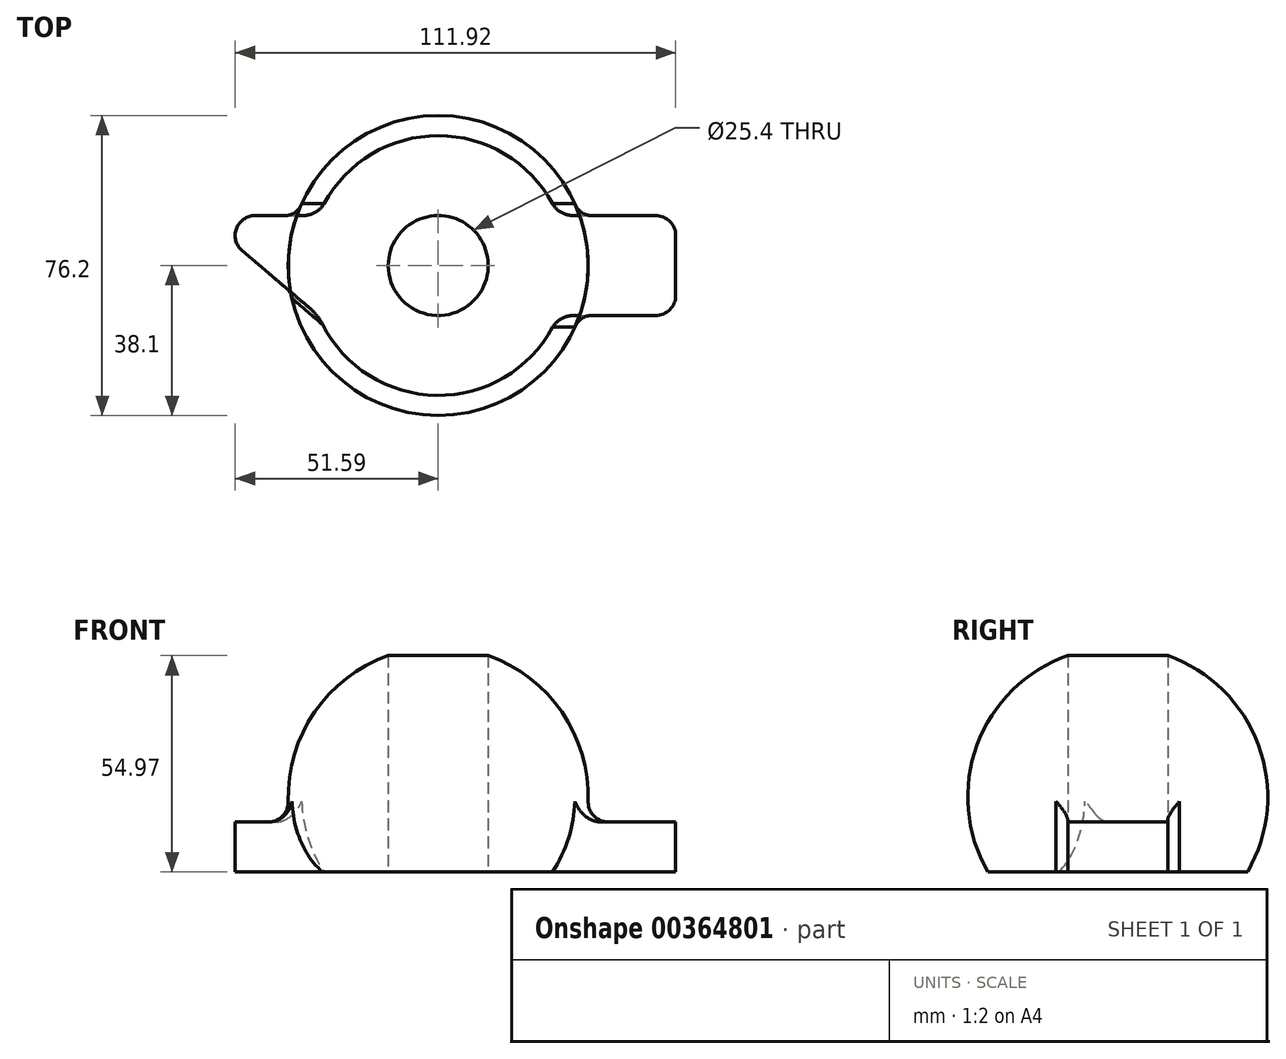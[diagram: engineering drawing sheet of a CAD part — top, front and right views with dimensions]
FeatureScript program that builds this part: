
annotation { "Feature Type Name" : "Feature", "Feature Type Description" : "" }
export const myFeature = defineFeature(function(context is Context, id is Id, definition is map)
    precondition{}
    {
        {
            var Q0;
            Q0=qCreatedBy(makeId("Front.planeOp"),FACE);
            var sketch = newSketch(context, id + "F0", { "sketchPlane" : qUnion([Q0])});
            skArc(sketch, "E0", {"start": v(33, -19.05) * mm, "mid": v(0, 38.1) * mm, "end": v(-33, -19.05) * mm});
            skLineSegment(sketch, "E1", {"start": v(-33, -19.05) * mm, "end": v(33, -19.05) * mm});
            skLineSegment(sketch, "E2", {"start": v(0, 0) * mm, "end": v(0, -19.05) * mm, "construction": true});
            skLineSegment(sketch, "E3", {"start": v(0, -19.05) * mm, "end": v(0, 38.1) * mm});
            skSolve(sketch);
        }
        {
            var Q0;
            {var subQ3=sQuery(id+"F0.wireOp",EDGE,"E3");Q0=makeQuery(id+"F0.imprint","IMPRINT",FACE,{"disambiguationData":[TD([[makeQuery(id+"F0.imprint","IMPRINT",EDGE,{"derivedFrom":subQ3}),-1.0]])]});}
            var Q1;
            Q1=sQuery(id+"F0.wireOp",EDGE,"E3");
            revolve(context, id + "F1", {"entities" : qUnion([Q0]), "axis" : qUnion([Q1]), "revolveType" : RevolveType.FULL});
        }
        {
            var Q0;
            Q0=qCreatedBy(makeId("Top.planeOp"),FACE);
            var sketch = newSketch(context, id + "F2", { "sketchPlane" : qUnion([Q0])});
            skCircle(sketch, "E4", {"center": v(0, 0) * mm, "radius": 12.7 * mm});
            skSolve(sketch);
        }
        {
            var Q0;
            Q0 = qSketchRegion(id + "F2", true);
            extrude(context, id + "F3", {"entities" : qUnion([Q0]), "operationType" : NewBodyOperationType.REMOVE, "endBound" : BoundingType.SYMMETRIC, "depth" : 152.4 * mm});
        }
        {
            var Q0;
            Q0=makeQuery(id+"F1.opRevolve","SWEPT_FACE",FACE,{"disambiguationData":[OSD([sQuery(id+"F0.wireOp",EDGE,"E1")])]});
            var sketch = newSketch(context, id + "F4", { "sketchPlane" : qUnion([Q0])});
            skLineSegment(sketch, "E5.bottom", {"start": v(60.33, -12.7) * mm, "end": v(-60.33, -12.7) * mm});
            skLineSegment(sketch, "E5.top", {"start": v(60.33, 12.7) * mm, "end": v(-60.33, 12.7) * mm});
            skLineSegment(sketch, "E5.left", {"start": v(60.33, -12.7) * mm, "end": v(60.33, 12.7) * mm});
            skLineSegment(sketch, "E5.right", {"start": v(-60.33, -12.7) * mm, "end": v(-60.33, 12.7) * mm});
            skPoint(sketch, "E5.middle", {"position": v(0, 0) * mm});
            skLineSegment(sketch, "E6", {"start": v(-30.45, 12.7) * mm, "end": v(-60.33, -12.7) * mm});
            skSolve(sketch);
        }
        {
            var Q0;
            {var subQ0=sQuery(id+"F4.wireOp",EDGE,"E5.left");Q0=makeQuery(id+"F4.imprint","IMPRINT",FACE,{"disambiguationData":[TD([[makeQuery(id+"F4.imprint","IMPRINT",EDGE,{"derivedFrom":subQ0}),1.0]])]});}
            var Q1;
            {var subQ0=sQuery(id+"F4.wireOp",EDGE,"E5.bottom");var subQ1=sQuery(id+"F0.wireOp",EDGE,"E1");var subQ2=makeQuery(id+"F1.opRevolve","SWEPT_EDGE",EDGE,{"disambiguationData":[OSD([sQuery(id+"F0.wireOp",EDGE,"E0"),subQ1])]});var subQ3=makeQuery(id+"F4.imprint","INTERSECT",VERTEX,{"disambiguationData":[OD(0.0)],"derivedFrom":[subQ2,subQ0]});Q1=makeQuery(id+"F4.imprint","IMPRINT",FACE,{"disambiguationData":[TD([[makeQuery(id+"F4.imprint","IMPRINT",EDGE,{"disambiguationData":[TD([[subQ3,-1.0]])],"derivedFrom":subQ0}),-1.0]])]});}
            var Q2;
            {var subQ0=sQuery(id+"F4.wireOp",EDGE,"E5.bottom");var subQ1=sQuery(id+"F0.wireOp",EDGE,"E1");var subQ2=makeQuery(id+"F1.opRevolve","SWEPT_EDGE",EDGE,{"disambiguationData":[OSD([sQuery(id+"F0.wireOp",EDGE,"E0"),subQ1])]});var subQ3=makeQuery(id+"F4.imprint","INTERSECT",VERTEX,{"disambiguationData":[OD(1.0)],"derivedFrom":[subQ2,subQ0]});Q2=makeQuery(id+"F4.imprint","IMPRINT",FACE,{"disambiguationData":[TD([[makeQuery(id+"F4.imprint","IMPRINT",EDGE,{"disambiguationData":[TD([[subQ3,1.0]])],"derivedFrom":subQ0}),-1.0]])]});}
            var Q3;
            {var subQ0=sQuery(id+"F4.wireOp",EDGE,"E6");Q3=makeQuery(id+"F4.imprint","IMPRINT",FACE,{"disambiguationData":[TD([[makeQuery(id+"F4.imprint","IMPRINT",EDGE,{"derivedFrom":subQ0}),1.0]])]});}
            extrude(context, id + "F5", {"entities" : qUnion([Q0, Q1, Q2, Q3]), "operationType" : NewBodyOperationType.ADD, "oppositeDirection" : true, "depth" : 12.7 * mm});
        }
        {
            var Q0;
            Q0=makeQuery(id+"F5.boolean.opBoolean","INTERSECT",EDGE,{"disambiguationData":[OD(1.0)],"derivedFrom":[makeQuery(id+"F1.opRevolve","SWEPT_FACE",FACE,{"disambiguationData":[OSD([sQuery(id+"F0.wireOp",EDGE,"E0")])]}),makeQuery(id+"F5.opExtrude","SWEPT_FACE",FACE,{"disambiguationData":[OSD([sQuery(id+"F4.wireOp",EDGE,"E5.top")])]})]});
            var Q1;
            Q1=makeQuery(id+"F5.boolean.opBoolean","INTERSECT",EDGE,{"disambiguationData":[OD(1.0)],"derivedFrom":[makeQuery(id+"F1.opRevolve","SWEPT_FACE",FACE,{"disambiguationData":[OSD([sQuery(id+"F0.wireOp",EDGE,"E0")])]}),makeQuery(id+"F5.opExtrude","CAP_FACE",FACE,{"disambiguationData":[OSD([sQuery(id+"F4.wireOp",EDGE,"E5.bottom"),sQuery(id+"F4.wireOp",EDGE,"E5.top"),sQuery(id+"F4.wireOp",EDGE,"E5.left"),sQuery(id+"F4.wireOp",EDGE,"E5.right")])],"isStart":false})]});
            var Q2;
            Q2=makeQuery(id+"F5.opExtrude","SWEPT_EDGE",EDGE,{"disambiguationData":[OSD([sQuery(id+"F4.wireOp",EDGE,"E5.top"),sQuery(id+"F4.wireOp",EDGE,"E5.right")])]});
            var Q3;
            Q3=makeQuery(id+"F5.opExtrude","SWEPT_EDGE",EDGE,{"disambiguationData":[OSD([sQuery(id+"F4.wireOp",EDGE,"E5.bottom"),sQuery(id+"F4.wireOp",EDGE,"E5.right")])]});
            var Q4;
            Q4=makeQuery(id+"F5.boolean.opBoolean","INTERSECT",EDGE,{"disambiguationData":[OD(1.0)],"derivedFrom":[makeQuery(id+"F1.opRevolve","SWEPT_FACE",FACE,{"disambiguationData":[OSD([sQuery(id+"F0.wireOp",EDGE,"E0")])]}),makeQuery(id+"F5.opExtrude","SWEPT_FACE",FACE,{"disambiguationData":[OSD([sQuery(id+"F4.wireOp",EDGE,"E5.bottom")])]})]});
            var Q5;
            Q5=makeQuery(id+"F5.boolean.opBoolean","INTERSECT",EDGE,{"disambiguationData":[OD(0.0)],"derivedFrom":[makeQuery(id+"F1.opRevolve","SWEPT_FACE",FACE,{"disambiguationData":[OSD([sQuery(id+"F0.wireOp",EDGE,"E0")])]}),makeQuery(id+"F5.opExtrude","SWEPT_FACE",FACE,{"disambiguationData":[OSD([sQuery(id+"F4.wireOp",EDGE,"E5.top")])]})]});
            var Q6;
            Q6=makeQuery(id+"F5.opExtrude","SWEPT_EDGE",EDGE,{"disambiguationData":[OSD([sQuery(id+"F4.wireOp",EDGE,"E5.top"),sQuery(id+"F4.wireOp",EDGE,"E5.left")])]});
            var Q7;
            Q7=makeQuery(id+"F5.opExtrude","SWEPT_EDGE",EDGE,{"disambiguationData":[OSD([sQuery(id+"F4.wireOp",EDGE,"E5.bottom"),sQuery(id+"F4.wireOp",EDGE,"E5.left")])]});
            var Q8;
            Q8=makeQuery(id+"F5.boolean.opBoolean","INTERSECT",EDGE,{"disambiguationData":[OD(0.0)],"derivedFrom":[makeQuery(id+"F1.opRevolve","SWEPT_FACE",FACE,{"disambiguationData":[OSD([sQuery(id+"F0.wireOp",EDGE,"E0")])]}),makeQuery(id+"F5.opExtrude","SWEPT_FACE",FACE,{"disambiguationData":[OSD([sQuery(id+"F4.wireOp",EDGE,"E5.bottom")])]})]});
            var Q9;
            Q9=makeQuery(id+"F5.boolean.opBoolean","INTERSECT",EDGE,{"disambiguationData":[OD(0.0)],"derivedFrom":[makeQuery(id+"F1.opRevolve","SWEPT_FACE",FACE,{"disambiguationData":[OSD([sQuery(id+"F0.wireOp",EDGE,"E0")])]}),makeQuery(id+"F5.opExtrude","CAP_FACE",FACE,{"disambiguationData":[OSD([sQuery(id+"F4.wireOp",EDGE,"E5.bottom"),sQuery(id+"F4.wireOp",EDGE,"E5.top"),sQuery(id+"F4.wireOp",EDGE,"E5.left"),sQuery(id+"F4.wireOp",EDGE,"E5.right")])],"isStart":false})]});
            fillet(context, id + "F6", {"entities" : qUnion([Q0, Q1, Q2, Q3, Q4, Q5, Q6, Q7, Q8, Q9]), "radius" : 5.08 * mm, "tangentPropagation" : true, "allowEdgeOverflow" : false});
        }
        {
            var Q0;
            Q0=makeQuery(id+"F5.boolean.opBoolean","INTERSECT",EDGE,{"derivedFrom":[makeQuery(id+"F1.opRevolve","SWEPT_FACE",FACE,{"disambiguationData":[OSD([sQuery(id+"F0.wireOp",EDGE,"E0")])]}),makeQuery(id+"F5.opExtrude","SWEPT_FACE",FACE,{"disambiguationData":[OSD([sQuery(id+"F4.wireOp",EDGE,"E6")])]})]});
            var Q1;
            Q1=makeQuery(id+"F5.boolean.opBoolean","INTERSECT",EDGE,{"derivedFrom":[makeQuery(id+"F1.opRevolve","SWEPT_FACE",FACE,{"disambiguationData":[OSD([sQuery(id+"F0.wireOp",EDGE,"E0")])]}),makeQuery(id+"F5.opExtrude","CAP_FACE",FACE,{"disambiguationData":[OSD([sQuery(id+"F0.wireOp",EDGE,"E1"),sQuery(id+"F2.wireOp",EDGE,"E4"),sQuery(id+"F4.wireOp",EDGE,"E5.bottom"),sQuery(id+"F4.wireOp",EDGE,"E5.top"),sQuery(id+"F4.wireOp",EDGE,"E6")])],"isStart":false})]});
            fillet(context, id + "F7", {"entities" : qUnion([Q0, Q1]), "radius" : 5.08 * mm, "tangentPropagation" : true, "allowEdgeOverflow" : false});
        }
    });
